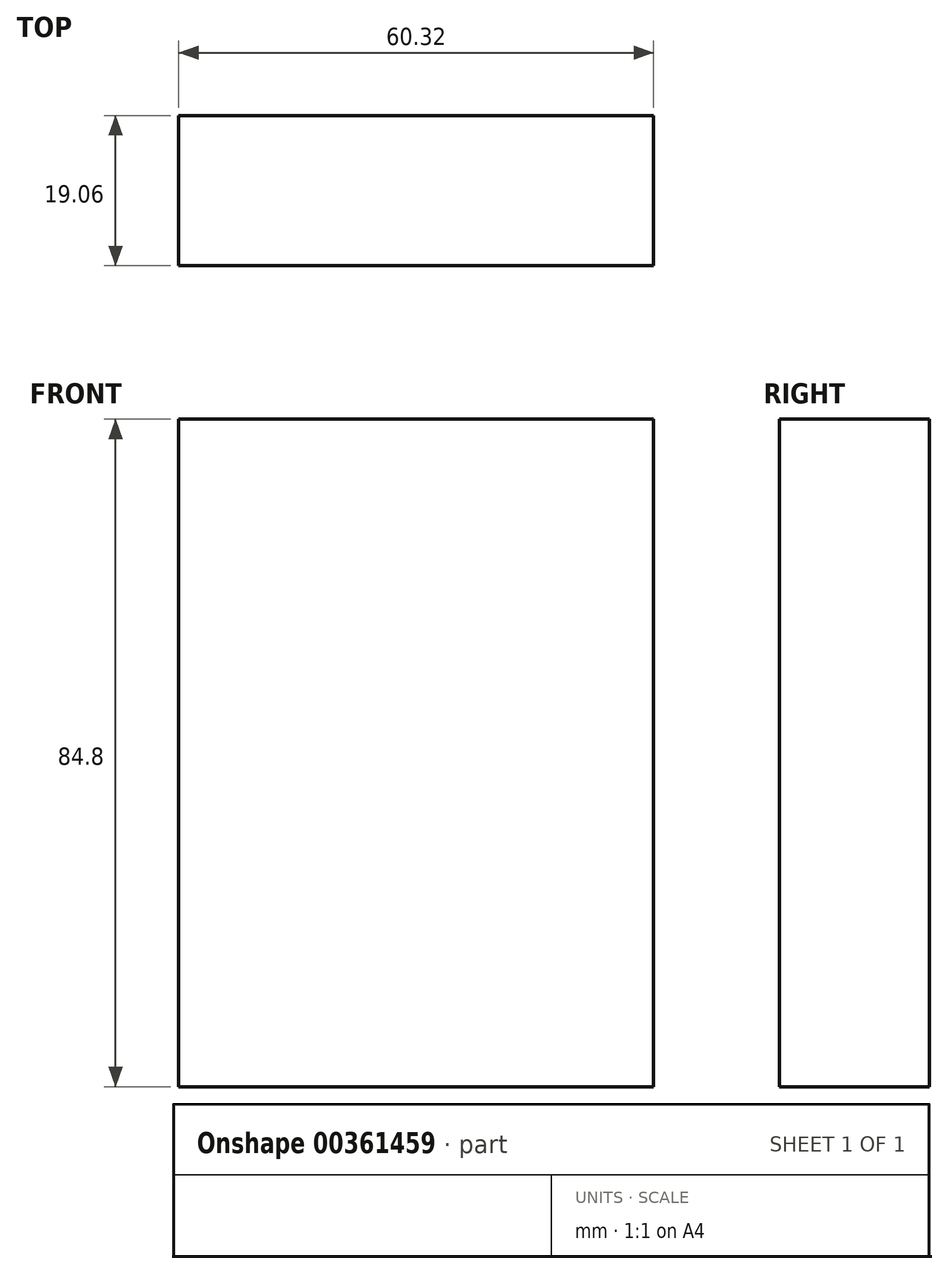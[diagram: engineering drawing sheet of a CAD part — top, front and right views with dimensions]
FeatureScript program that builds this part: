
annotation { "Feature Type Name" : "Feature", "Feature Type Description" : "" }
export const myFeature = defineFeature(function(context is Context, id is Id, definition is map)
    precondition{}
    {
        {
            var Q0;
            Q0=qCreatedBy(makeId("Front.planeOp"),FACE);
            var sketch = newSketch(context, id + "F0", { "sketchPlane" : qUnion([Q0])});
            skLineSegment(sketch, "E0.bottom", {"start": v(30.16, -42.4) * mm, "end": v(-30.16, -42.4) * mm});
            skLineSegment(sketch, "E0.top", {"start": v(30.16, 42.4) * mm, "end": v(-30.16, 42.4) * mm});
            skLineSegment(sketch, "E0.left", {"start": v(30.16, -42.4) * mm, "end": v(30.16, 42.4) * mm});
            skLineSegment(sketch, "E0.right", {"start": v(-30.16, -42.4) * mm, "end": v(-30.16, 42.4) * mm});
            skPoint(sketch, "E0.middle", {"position": v(0, 0) * mm});
            skSolve(sketch);
        }
        {
            var Q0;
            Q0 = qSketchRegion(id + "F0", true);
            extrude(context, id + "F1", {"entities" : qUnion([Q0]), "endBound" : BoundingType.SYMMETRIC, "depth" : 19.05 * mm});
        }
    });
